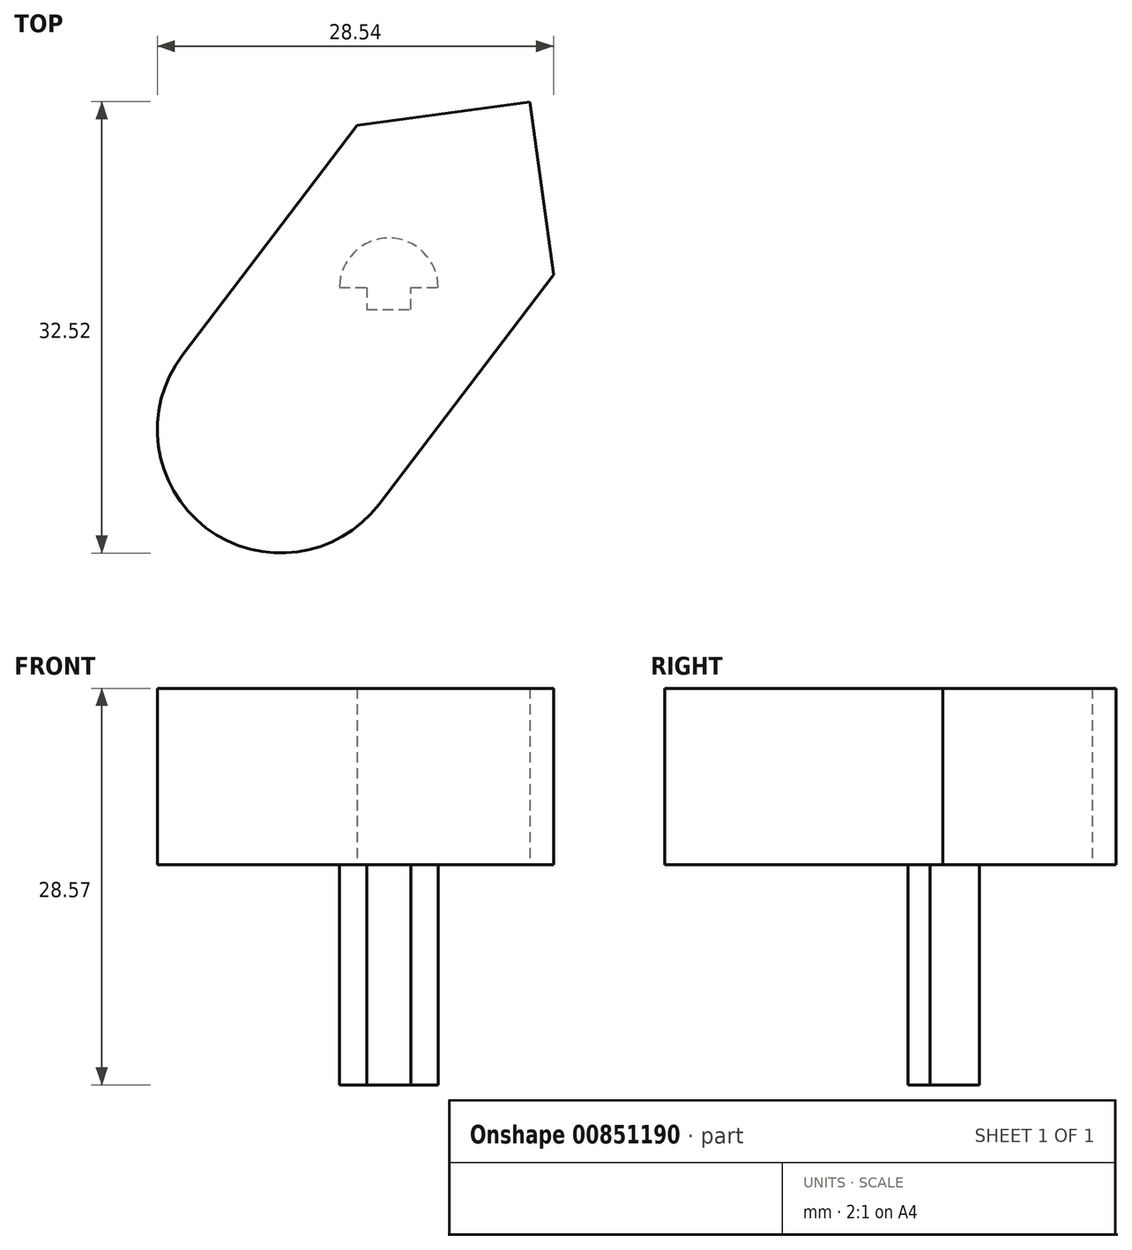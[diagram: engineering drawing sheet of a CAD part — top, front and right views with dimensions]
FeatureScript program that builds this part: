
annotation { "Feature Type Name" : "Feature", "Feature Type Description" : "" }
export const myFeature = defineFeature(function(context is Context, id is Id, definition is map)
    precondition{}
    {
        {
            var Q0;
            Q0=qCreatedBy(makeId("Top.planeOp"),FACE);
            var sketch = newSketch(context, id + "F0", { "sketchPlane" : qUnion([Q0])});
            skArc(sketch, "E0", {"start": v(-3.56, 0) * mm, "mid": v(0, 3.56) * mm, "end": v(3.56, 0) * mm});
            skLineSegment(sketch, "E1", {"start": v(-3.56, 0) * mm, "end": v(-1.59, 0) * mm});
            skLineSegment(sketch, "E2", {"start": v(-1.59, 0) * mm, "end": v(-1.59, -1.59) * mm});
            skLineSegment(sketch, "E3", {"start": v(-1.59, -1.59) * mm, "end": v(1.59, -1.59) * mm});
            skLineSegment(sketch, "E4", {"start": v(1.59, -1.59) * mm, "end": v(1.59, 0) * mm});
            skLineSegment(sketch, "E5", {"start": v(1.59, 0) * mm, "end": v(3.56, 0) * mm});
            skCircle(sketch, "E6", {"center": v(0, 0) * mm, "radius": 6.35 * mm});
            skSolve(sketch);
        }
        {
            var Q0;
            Q0=makeQuery(id+"F0.imprint","IMPRINT",FACE,{"disambiguationData":[TD([[makeQuery(id+"F0.imprint","IMPRINT",EDGE,{"derivedFrom":sQuery(id+"F0.wireOp",EDGE,"E0")}),1.0]])]});
            extrude(context, id + "F1", {"entities" : qUnion([Q0]), "depth" : 15.88 * mm, "offsetDistance" : 25.4 * mm});
        }
        {
            var Q0;
            Q0=makeQuery(id+"F1.opExtrude","CAP_FACE",FACE,{"disambiguationData":[OSD([sQuery(id+"F0.wireOp",EDGE,"E0"),sQuery(id+"F0.wireOp",EDGE,"E1"),sQuery(id+"F0.wireOp",EDGE,"E2"),sQuery(id+"F0.wireOp",EDGE,"E3"),sQuery(id+"F0.wireOp",EDGE,"E4"),sQuery(id+"F0.wireOp",EDGE,"E5"),sQuery(id+"F0.wireOp",EDGE,"E6")])],"isStart":false});
            var sketch = newSketch(context, id + "F2", { "sketchPlane" : qUnion([Q0])});
            skLineSegment(sketch, "E7", {"start": v(10.16, 13.38) * mm, "end": v(-13.16, -17.33) * mm});
            skLineSegment(sketch, "E8", {"start": v(-13.16, -17.33) * mm, "end": v(-13.16, -17.33) * mm});
            skLineSegment(sketch, "E9", {"start": v(-14.86, -4.87) * mm, "end": v(3.08, 18.75) * mm});
            skLineSegment(sketch, "E10", {"start": v(3.08, 18.75) * mm, "end": v(10.16, 13.38) * mm});
            skLineSegment(sketch, "E11.MirrorCS", {"start": v(-0.7, -15.63) * mm, "end": v(17.24, 8) * mm});
            skLineSegment(sketch, "E12.MirrorCS", {"start": v(17.24, 8) * mm, "end": v(10.16, 13.38) * mm});
            skPoint(sketch, "E13.visualSharp", {"position": v(-6.08, -22.7) * mm});
            skArc(sketch, "E13.filletArc", {"start": v(-13.16, -17.33) * mm, "mid": v(-6.58, -19.06) * mm, "end": v(-0.7, -15.63) * mm});
            skPoint(sketch, "E14.visualSharp", {"position": v(-20.24, -11.95) * mm});
            skArc(sketch, "E14.filletArc", {"start": v(-14.86, -4.87) * mm, "mid": v(-16.6, -11.45) * mm, "end": v(-13.16, -17.33) * mm});
            skSolve(sketch);
        }
        {
            var Q0;
            Q0 = qSketchRegion(id + "F2", true);
            extrude(context, id + "F3", {"entities" : qUnion([Q0]), "operationType" : NewBodyOperationType.ADD, "depth" : 12.7 * mm, "offsetDistance" : 25.4 * mm});
        }
        {
            var Q0;
            Q0=makeQuery(id+"F3.opExtrude","SWEPT_EDGE",EDGE,{"disambiguationData":[OSD([sQuery(id+"F2.wireOp",EDGE,"E9"),sQuery(id+"F2.wireOp",EDGE,"E10")])]});
            var Q1;
            Q1=makeQuery(id+"F3.opExtrude","SWEPT_EDGE",EDGE,{"disambiguationData":[OSD([sQuery(id+"F2.wireOp",EDGE,"E11.MirrorCS"),sQuery(id+"F2.wireOp",EDGE,"E12.MirrorCS")])]});
            chamfer(context, id + "F4", {"entities" : qUnion([Q0, Q1]), "width" : 8.9 * mm, "tangentPropagation" : true});
        }
    });
